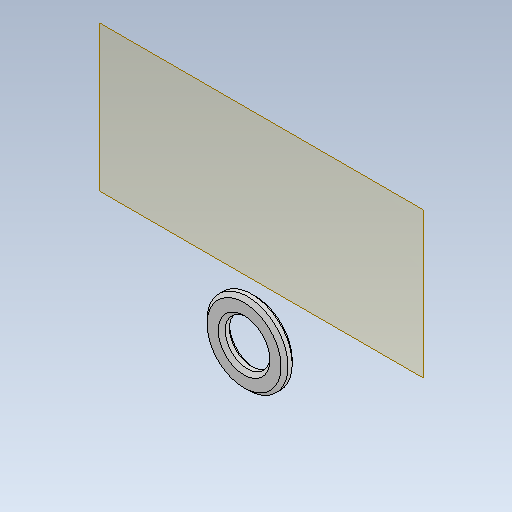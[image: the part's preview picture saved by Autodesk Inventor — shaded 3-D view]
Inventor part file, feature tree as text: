
AUTODESK INVENTOR PART (.ipt)
format: ipt  version: 2023 (Build 270158030, 158C)  size: 111,616 bytes
history: native  units: mm
features: other x4, chamfer x2, reference x2, plane x1, extrude x1, sketch x1
ambient origin geometry x8: Origin, YZ Plane, XZ Plane, XY Plane, X Axis, Y Axis, Z Axis, Center Point
bodies: Body1 (feature_tree)
feature tree (11):
  other  "washer"
  plane  "Work Plane1"
  extrude  "Extrusion1"  Depth=1.6mm TaperAngle=0.0deg
  chamfer  "Chamfer1"  Distance=0.5mm Angle=45.0deg
  chamfer  "Chamfer2"  Distance=6.4mm
  sketch  "Sketch1"  dims[d0=1.8mm d1=1.6mm d2=0.0mm d3=0.5mm d4=2.0mm d5=45.0deg d6=6.4mm d7=0.5mm d8=2.0mm d9=45.0deg]
  reference  "Reference1"
  reference  "Reference2"
  other  "<userpath>\Documents\0004-inventor\3D-CAD-main\trebuchet\trebuchet-assembly.iam"
  other  "trebuchet-assembly.iam"
  other  "v1-counterweight:1"
